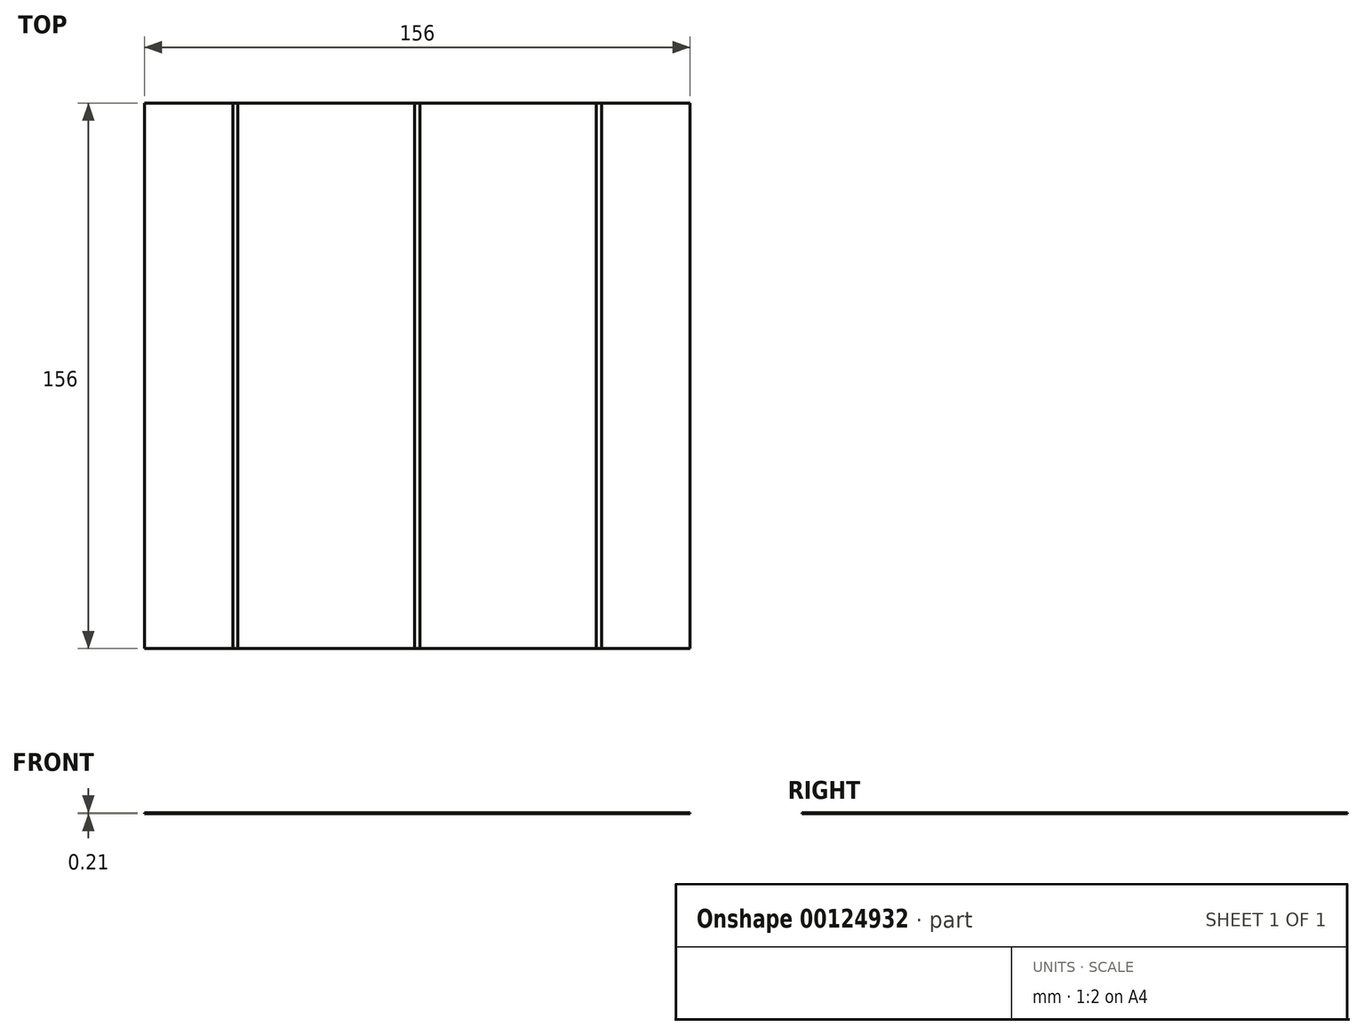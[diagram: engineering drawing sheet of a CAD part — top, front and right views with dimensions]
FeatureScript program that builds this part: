
annotation { "Feature Type Name" : "Feature", "Feature Type Description" : "" }
export const myFeature = defineFeature(function(context is Context, id is Id, definition is map)
    precondition{}
    {
        {
            var Q0;
            Q0=qCreatedBy(makeId("Top.planeOp"),FACE);
            var sketch = newSketch(context, id + "F0", { "sketchPlane" : qUnion([Q0])});
            skLineSegment(sketch, "E0.bottom", {"start": v(0, 0) * mm, "end": v(156, 0) * mm});
            skLineSegment(sketch, "E0.top", {"start": v(0, 156) * mm, "end": v(156, 156) * mm});
            skLineSegment(sketch, "E0.left", {"start": v(0, 0) * mm, "end": v(0, 156) * mm});
            skLineSegment(sketch, "E0.right", {"start": v(156, 0) * mm, "end": v(156, 156) * mm});
            skSolve(sketch);
        }
        {
            var Q0;
            Q0 = qSketchRegion(id + "F0", true);
            extrude(context, id + "F1", {"entities" : qUnion([Q0]), "depth" : 0.2 * mm});
        }
        {
            var Q0;
            Q0=makeQuery(id+"F1.opExtrude","CAP_FACE",FACE,{"disambiguationData":[OSD([sQuery(id+"F0.wireOp",EDGE,"E0.bottom"),sQuery(id+"F0.wireOp",EDGE,"E0.top"),sQuery(id+"F0.wireOp",EDGE,"E0.left"),sQuery(id+"F0.wireOp",EDGE,"E0.right")])],"isStart":false});
            var sketch = newSketch(context, id + "F2", { "sketchPlane" : qUnion([Q0])});
            skLineSegment(sketch, "E1.bottom", {"start": v(25.25, 0) * mm, "end": v(26.75, 0) * mm});
            skLineSegment(sketch, "E1.top", {"start": v(25.25, 156) * mm, "end": v(26.75, 156) * mm});
            skLineSegment(sketch, "E1.left", {"start": v(25.25, 0) * mm, "end": v(25.25, 156) * mm});
            skLineSegment(sketch, "E1.right", {"start": v(26.75, 0) * mm, "end": v(26.75, 156) * mm});
            skLineSegment(sketch, "E2.bottom", {"start": v(77.25, 156) * mm, "end": v(78.75, 156) * mm});
            skLineSegment(sketch, "E2.top", {"start": v(77.25, 0) * mm, "end": v(78.75, 0) * mm});
            skLineSegment(sketch, "E2.left", {"start": v(77.25, 156) * mm, "end": v(77.25, 0) * mm});
            skLineSegment(sketch, "E2.right", {"start": v(78.75, 156) * mm, "end": v(78.75, 0) * mm});
            skLineSegment(sketch, "E3.bottom", {"start": v(129.25, 0) * mm, "end": v(130.75, 0) * mm});
            skLineSegment(sketch, "E3.top", {"start": v(129.25, 156) * mm, "end": v(130.75, 156) * mm});
            skLineSegment(sketch, "E3.left", {"start": v(129.25, 0) * mm, "end": v(129.25, 156) * mm});
            skLineSegment(sketch, "E3.right", {"start": v(130.75, 0) * mm, "end": v(130.75, 156) * mm});
            skSolve(sketch);
        }
        {
            var Q0;
            Q0 = qSketchRegion(id + "F2", true);
            extrude(context, id + "F3", {"entities" : qUnion([Q0]), "depth" : 0.01 * mm});
        }
    });
